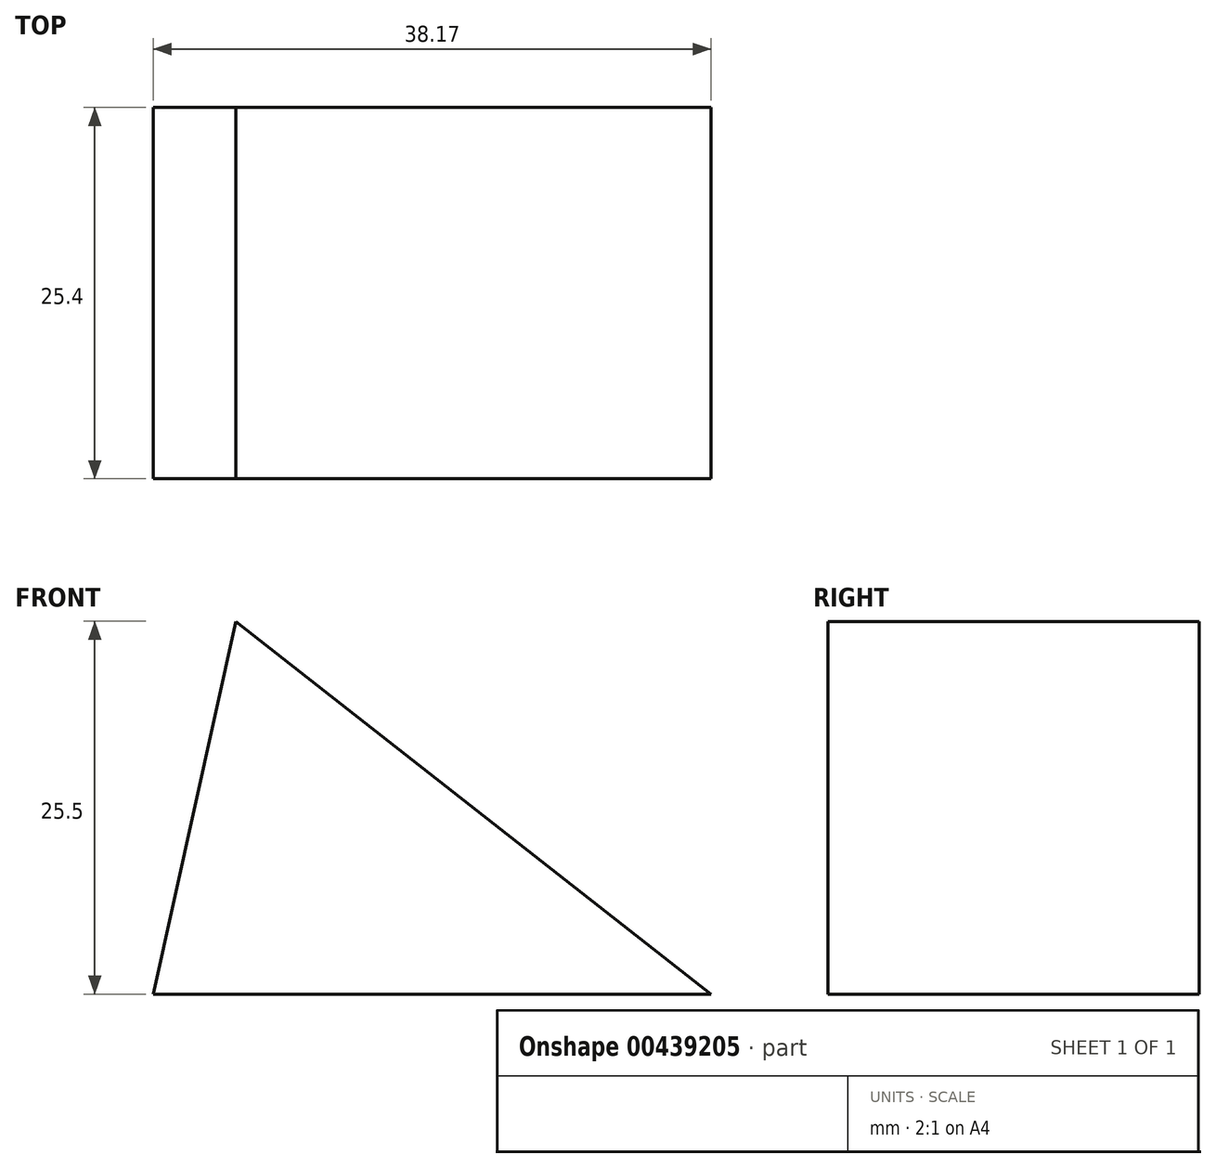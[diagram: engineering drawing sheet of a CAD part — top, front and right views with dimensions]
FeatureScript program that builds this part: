
annotation { "Feature Type Name" : "Feature", "Feature Type Description" : "" }
export const myFeature = defineFeature(function(context is Context, id is Id, definition is map)
    precondition{}
    {
        {
            var Q0;
            Q0=qCreatedBy(makeId("Front.planeOp"),FACE);
            var sketch = newSketch(context, id + "F0", { "sketchPlane" : qUnion([Q0])});
            skLineSegment(sketch, "E0", {"start": v(75.31, 70.27) * mm, "end": v(60.88, 44.25) * mm});
            skLineSegment(sketch, "E1", {"start": v(60.88, 44.25) * mm, "end": v(20.6, 52.56) * mm});
            skLineSegment(sketch, "E2", {"start": v(20.6, 52.56) * mm, "end": v(46.23, 39.3) * mm});
            skLineSegment(sketch, "E3", {"start": v(46.23, 39.3) * mm, "end": v(0, 15.43) * mm});
            skLineSegment(sketch, "E4", {"start": v(0, 15.43) * mm, "end": v(58.46, 0) * mm});
            skLineSegment(sketch, "E5", {"start": v(58.46, 0) * mm, "end": v(25.94, 0.36) * mm});
            skLineSegment(sketch, "E6", {"start": v(25.94, 0.36) * mm, "end": v(58.46, -25.14) * mm});
            skLineSegment(sketch, "E7", {"start": v(58.46, -25.14) * mm, "end": v(42.2, -25.14) * mm});
            skPoint(sketch, "E7.endSnap0", {"position": v(42.2, -12.4) * mm});
            skLineSegment(sketch, "E8", {"start": v(42.2, -25.14) * mm, "end": v(20.29, -25.14) * mm});
            skLineSegment(sketch, "E9", {"start": v(20.29, -25.14) * mm, "end": v(25.94, 0.36) * mm});
            skSolve(sketch);
        }
        {
            var Q0;
            Q0 = qSketchRegion(id + "F0", true);
            extrude(context, id + "F1", {"entities" : qUnion([Q0]), "depth" : 25.4 * mm});
        }
    });
